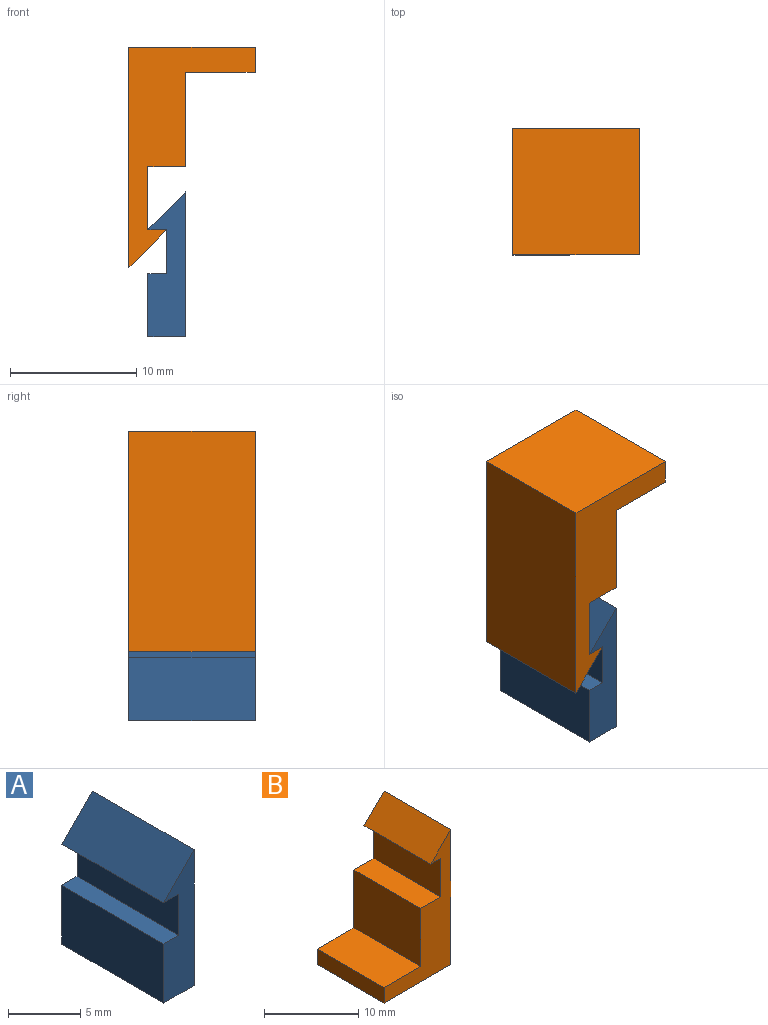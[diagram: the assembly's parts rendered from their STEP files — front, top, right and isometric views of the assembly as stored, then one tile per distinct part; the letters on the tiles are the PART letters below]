
ASSEMBLY  parts=2 mates=1
PART A: 9 faces, bbox 3x10x11.5 mm
  f0: plane 11.5x3mm, normal (0,-1,0), area 24.7mm2, adj f1,f3,f4,f5,f6,f7,f8
  f1: plane 11.5x10mm, normal (1,0,0), area 115mm2, adj f0,f2,f5,f8
  f2: plane 11.5x3mm, normal (0,1,0), area 24.7mm2, adj f1,f3,f4,f5,f6,f7,f8
  f3: plane 10x5mm, normal (-1,0,0), area 50mm2, adj f0,f2,f4,f5
  f4: plane 10x1.5mm, normal (0,0,1), area 15mm2, adj f0,f2,f3,f6
  f5: plane 10x3mm, normal (0,0,-1), area 30mm2, adj f0,f1,f2,f3
  f6: plane 10x3.5mm, normal (-1,0,0), area 35mm2, adj f0,f2,f4,f7
  f7: plane 10x1.5mm, normal (0,0,-1), area 15mm2, adj f0,f2,f6,f8
  f8: plane 10x3mm, normal (-0.71,0,0.71), area 42.4mm2, adj f0,f1,f2,f7
PART B: 11 faces, bbox 10x10x17.5 mm
  f0: plane 17.5x10mm, normal (0,-1,0), area 65.8mm2, adj f1,f3,f4,f5,f6,f7,f8,f9
  f1: plane 17.5x10mm, normal (1,0,0), area 175mm2, adj f0,f2,f5,f10
  f2: plane 17.5x10mm, normal (0,1,0), area 65.8mm2, adj f1,f3,f4,f5,f6,f7,f8,f9
  f3: plane 10x2mm, normal (-1,0,0), area 20mm2, adj f0,f2,f4,f5
  f4: plane 10x5.5mm, normal (0,0,1), area 55mm2, adj f0,f2,f3,f6
  f5: plane 10x10mm, normal (0,0,-1), area 100mm2, adj f0,f1,f2,f3
  f6: plane 10x7.5mm, normal (-1,0,0), area 75mm2, adj f0,f2,f4,f7
  f7: plane 10x3mm, normal (0,0,1), area 30mm2, adj f0,f2,f6,f8
  f8: plane 10x5mm, normal (-1,0,0), area 50mm2, adj f0,f2,f7,f9
  f9: plane 10x1.5mm, normal (0,0,-1), area 15mm2, adj f0,f2,f8,f10
  f10: plane 10x3mm, normal (-0.71,0,0.71), area 42.4mm2, adj f0,f1,f2,f9
PLACE A t=(3.13,3.5,-10.15)mm
PLACE B rot(axis=(0,-1,0),180deg) t=(5.13,3.5,12.85)mm
MATE fastened A.f7 <-> B.f9  axis (0,0,-1) through (2.38,3.5,-1.65)mm
